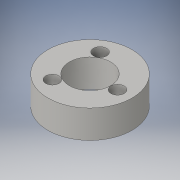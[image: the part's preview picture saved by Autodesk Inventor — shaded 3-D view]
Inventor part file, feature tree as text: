
AUTODESK INVENTOR PART (.ipt)
format: ipt  version: 2016 (Build 200138000, 138)  size: 105,984 bytes
history: native  units: in
note: dims shown in document units (in); Inventor stores cm internally (conversion verified against a paired STEP export)
features: extrude x2, sketch x2
ambient origin geometry x8: Origin, YZ Plane, XZ Plane, XY Plane, X Axis, Y Axis, Z Axis, Center Point
bodies: Solid1 (feature_tree)
feature tree (4):
  extrude  "Extrusion1"  Depth=1.5795in TaperAngle=360.0deg
  extrude  "Extrusion2"  [1 undecoded]
  sketch  "Sketch1"  dims[d5=1.5795in d6=0.0in d11=1.1811in d13=360.0deg]
  sketch  "Sketch2"  dims[d16=1.5795in d17=0.0in]
note: 1 required parameter value undecoded (feature->parameter linkage not recoverable at this tier; creation-order binding heuristic only, values carry confidence <= 0.55)
